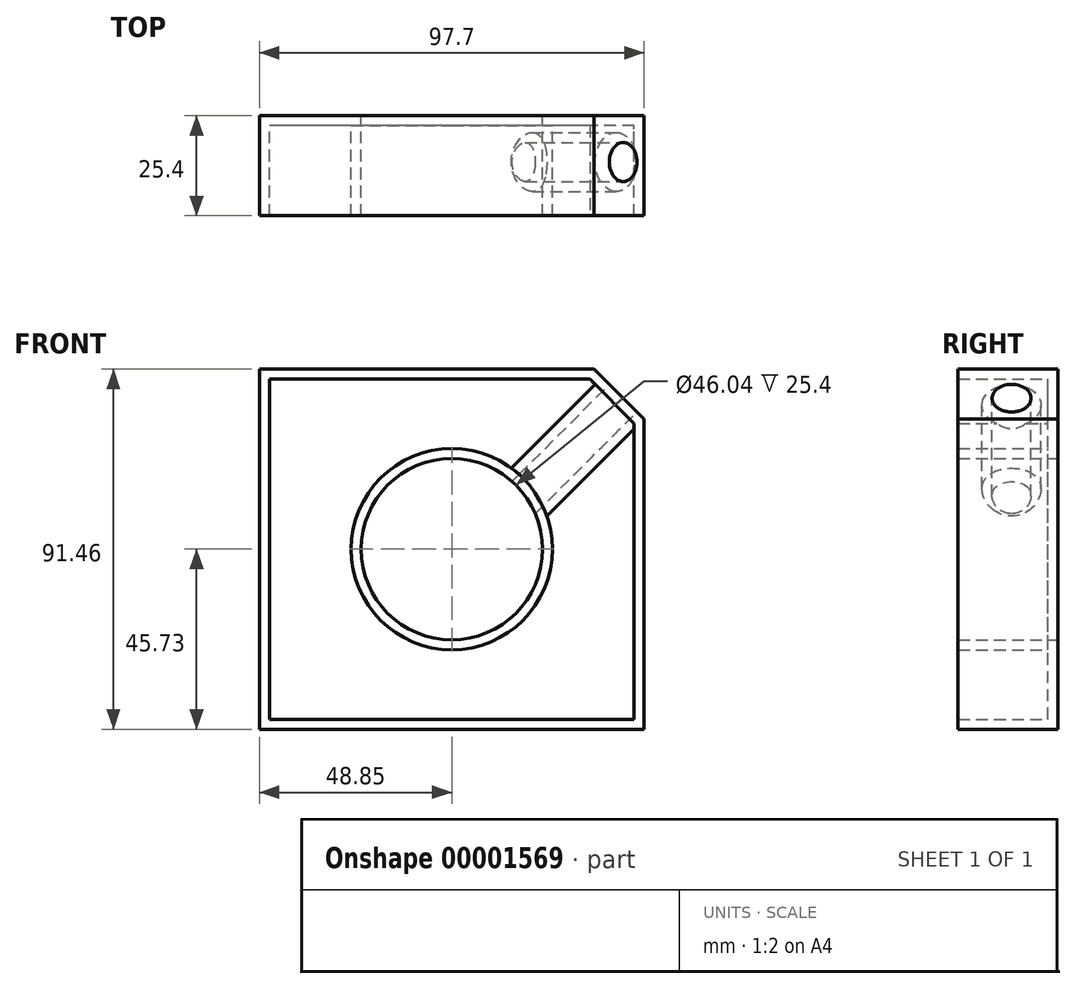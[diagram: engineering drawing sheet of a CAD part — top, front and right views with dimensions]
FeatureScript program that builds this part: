
annotation { "Feature Type Name" : "Feature", "Feature Type Description" : "" }
export const myFeature = defineFeature(function(context is Context, id is Id, definition is map)
    precondition{}
    {
        {
            var Q0;
            Q0=qCreatedBy(makeId("Front.planeOp"),FACE);
            var sketch = newSketch(context, id + "F0", { "sketchPlane" : qUnion([Q0])});
            skLineSegment(sketch, "E0.rect.bottom", {"start": v(48.85, -45.73) * mm, "end": v(-48.85, -45.73) * mm});
            skLineSegment(sketch, "E0.rect.top", {"start": v(48.85, 45.73) * mm, "end": v(-48.85, 45.73) * mm});
            skLineSegment(sketch, "E0.rect.left", {"start": v(48.85, -45.73) * mm, "end": v(48.85, 45.73) * mm});
            skLineSegment(sketch, "E0.rect.right", {"start": v(-48.85, -45.73) * mm, "end": v(-48.85, 45.73) * mm});
            skPoint(sketch, "E0.rect.middle", {"position": v(0, 0) * mm});
            skCircle(sketch, "E1", {"center": v(0, 0) * mm, "radius": 23.02 * mm});
            skSolve(sketch);
        }
        {
            var Q0;
            Q0 = qSketchRegion(id + "F0", true);
            extrude(context, id + "F1", {"entities" : qUnion([Q0]), "depth" : 25.4 * mm});
        }
        {
            var Q0;
            Q0=makeQuery(id+"F1.opExtrude","SWEPT_EDGE",EDGE,{"disambiguationData":[OSD([sQuery(id+"F0.wireOp",EDGE,"E0.rect.top"),sQuery(id+"F0.wireOp",EDGE,"E0.rect.left")])]});
            chamfer(context, id + "F2", {"entities" : qUnion([Q0]), "width" : 12.7 * mm, "tangentPropagation" : true});
        }
        {
            var Q0;
            Q0=makeQuery(id+"F2.opChamfer","BLEND_FACE",FACE,{"disambiguationData":[OSD([sQuery(id+"F0.wireOp",EDGE,"E0.rect.top"),sQuery(id+"F0.wireOp",EDGE,"E0.rect.left")])]});
            var sketch = newSketch(context, id + "F3", { "sketchPlane" : qUnion([Q0])});
            skCircle(sketch, "E2", {"center": v(-11.76, -3.65) * mm, "radius": 4.96 * mm});
            skSolve(sketch);
        }
        {
            var Q0;
            Q0 = qSketchRegion(id + "F3", true);
            extrude(context, id + "F4", {"entities" : qUnion([Q0]), "operationType" : NewBodyOperationType.REMOVE, "oppositeDirection" : true, "depth" : 56.42 * mm});
        }
        {
            var Q0;
            Q0=makeQuery(id+"F1.opExtrude","CAP_FACE",FACE,{"disambiguationData":[OSD([sQuery(id+"F0.wireOp",EDGE,"E0.rect.bottom"),sQuery(id+"F0.wireOp",EDGE,"E0.rect.top"),sQuery(id+"F0.wireOp",EDGE,"E0.rect.left"),sQuery(id+"F0.wireOp",EDGE,"E0.rect.right"),sQuery(id+"F0.wireOp",EDGE,"E1")])],"isStart":false});
            shell(context, id + "F5", {"entities" : qUnion([Q0]), "thickness" : 2.54 * mm});
        }
    });
